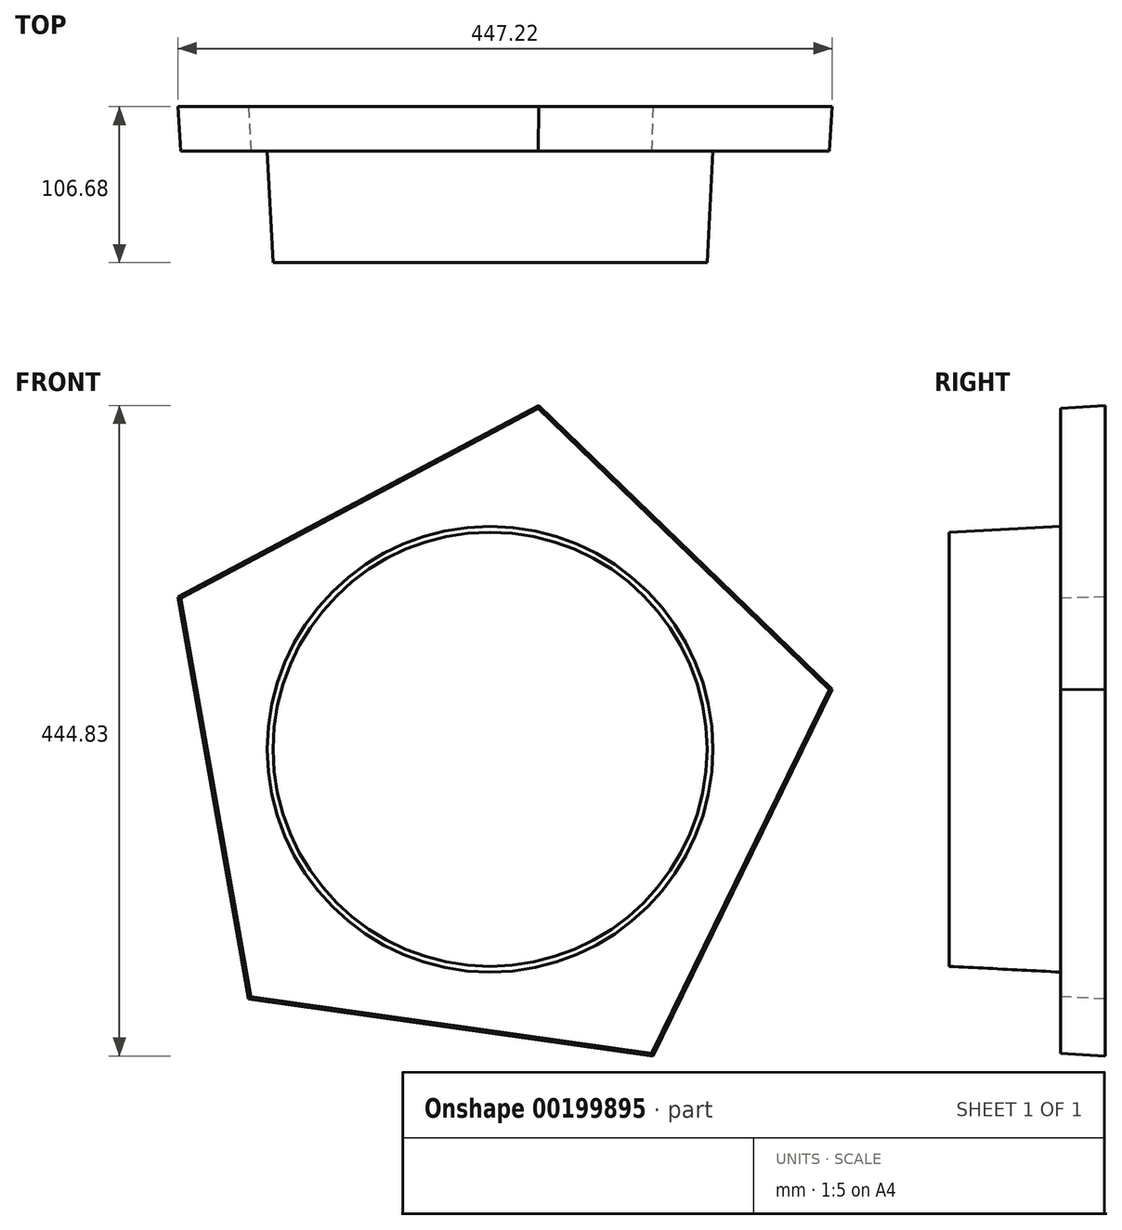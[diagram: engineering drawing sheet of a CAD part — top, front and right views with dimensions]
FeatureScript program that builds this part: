
annotation { "Feature Type Name" : "Feature", "Feature Type Description" : "" }
export const myFeature = defineFeature(function(context is Context, id is Id, definition is map)
    precondition{}
    {
        {
            var Q0;
            Q0=qCreatedBy(makeId("Front.planeOp"),FACE);
            var sketch = newSketch(context, id + "F0", { "sketchPlane" : qUnion([Q0])});
            skCircle(sketch, "E0.cCircle", {"center": v(0, 0) * mm, "radius": 190.5 * mm, "construction": true});
            skLineSegment(sketch, "E0.0", {"start": v(231.92, 40.76) * mm, "end": v(110.43, -207.97) * mm});
            skLineSegment(sketch, "E0.1", {"start": v(110.43, -207.97) * mm, "end": v(-163.66, -169.3) * mm});
            skLineSegment(sketch, "E0.2", {"start": v(-163.66, -169.3) * mm, "end": v(-211.58, 103.34) * mm});
            skLineSegment(sketch, "E0.3", {"start": v(-211.58, 103.34) * mm, "end": v(32.9, 233.16) * mm});
            skLineSegment(sketch, "E0.4", {"start": v(32.9, 233.16) * mm, "end": v(231.92, 40.76) * mm});
            skPoint(sketch, "E0.0.midPoint", {"position": v(171.18, -83.6) * mm});
            skSolve(sketch);
        }
        {
            var Q0;
            Q0 = qSketchRegion(id + "F0", true);
            extrude(context, id + "F1", {"entities" : qUnion([Q0]), "oppositeDirection" : true, "depth" : 30.48 * mm, "hasDraft" : true, "draftAngle" : 3 * degree});
        }
        {
            var Q0;
            Q0=makeQuery(id+"F1.opExtrude","CAP_FACE",FACE,{"disambiguationData":[OSD([sQuery(id+"F0.wireOp",EDGE,"E0.0"),sQuery(id+"F0.wireOp",EDGE,"E0.1"),sQuery(id+"F0.wireOp",EDGE,"E0.2"),sQuery(id+"F0.wireOp",EDGE,"E0.3"),sQuery(id+"F0.wireOp",EDGE,"E0.4")])],"isStart":true});
            var sketch = newSketch(context, id + "F2", { "sketchPlane" : qUnion([Q0])});
            skCircle(sketch, "E1", {"center": v(0, 0) * mm, "radius": 152.4 * mm});
            skSolve(sketch);
        }
        {
            var Q0;
            Q0 = qSketchRegion(id + "F2", true);
            extrude(context, id + "F3", {"entities" : qUnion([Q0]), "operationType" : NewBodyOperationType.ADD, "depth" : 76.2 * mm, "hasDraft" : true, "draftAngle" : 3 * degree, "draftPullDirection" : true});
        }
    });
